# Revit family: IS_Cerasprint_B9576_BIM_FR
name_source: partatom
category: Plumbing Fixtures
revit_build: Autodesk Revit 2017 (Build: 20160225_1515(x64)
units: mm (PartAtom-declared; Revit-internal decimal feet)

## family parameters
Always vertical = No
Cut with Voids When Loaded = No
OmniClass Number = 23.45.55.17
OmniClass Title = Mixing Faucets
Part Type = Normal
Room Calculation Point = No
Round Connector Dimension = Use Diameter
Shared = No
Work Plane-Based = No

## types (1)
- B9576AA - CERASPRINT MIT EVIER BEC TUBE 230MM CHR
    Accessoires = www.idealspec.fr
    Auteur = Ideal Standard
    BIMobject category = Taps & Mixers
    BIMobject category code = kitchen-taps
    BIMobject main category = Kitchen
    BIMobject main category code = kitchen
    BOSUseNativeGeometries = 1
    Bim-NomDuProjet = ISI_IdealStandard_SinkWaterSupplyFittings_CERASPRINT_B9576AA
    Brand url = www.idealspec.fr
    Caractéristiques = CERASPRINT SNK MXR R-MTD TUB/SPT U230MM
    CodeBarre = 3800861026952
    Conformité = NF
    ConseilsDInstallation = 0
    Cost = 0 $
    Couleur = Chrome
    CoûtDeRemplacement = 0
    Date of publishing = 2018_07_24
    DateDeCréation = 2018_07_24
    Description = CERASPRINT Mitigeur évier monotrou
    Dimensions = 306 x 85 x 251mm
    EAN code = https://3800861026952
    Edition number = 1
    Espace = Interne
    Finition = Chrome
    Forme = Complexe
    Hauteur = 306 mm  [stored 1.00394 ft]
    IFC Classification = Sanitary Terminal
    IfcExportAs = FAUCETS
    IfcExportType = IfcValveType
    InformationsProduit = www.idealspec.fr
    Installation instructions = http://www.idealspec.fr
    Largeur = 85 mm
    Longueur = 251 mm
    Manufacturer name = Ideal Standard
    Marque = Ideal Standard
    Material main = Brass
    Matériel = Brass
    Model = B9576AA
    NBS Reference Code = 35-79-79
    NBS Reference Description = Sink Water Supply Fittings
    Nominal height = 306
    Nominal width = 84
    OmniClass Code = 23-31 11 00
    OmniClass Description = Faucets
    Product Guid = 93ca3ec0-5324-4a6a-9915-9a6a16119ddc
    Product SKU = B9576
    Product certification = http://www.idealspec.fr
    Product data url = https://bimobject.com
    Product family = CERASPRINT
    Product group = Kitchen Mixer
    Product name = CERASPRINT SNK MXR R-MTD TUB/SPT U230MM
    Product url = http://www.idealspec.fr
    Profondeur = 0 mm  [stored 0 ft]
    QR code = http://bimobject.com
    Raccordement = Plomberie
    Révision = 1
    Technical description = http://www.idealspec.fr
    TestDePression = 0
    TypeDeRobinetterie = Sink Mixer
    URL = www.idealspec.fr
    Uniclass 1.4 Code = L8212
    Uniclass 1.4 Description = Fittings
    Uniclass 2.0 Code = PR-35-79-79
    Uniclass 2.0 Description = Sink Water Supply Fittings
    Uniclass 2015 Code = Pr_40_20_87_82
    Uniclass 2015 Name = Sink manual water supply sets
    Uniclass2015Code = Pr_40_20_87_82
    Uniclass2015Title = Sink manual water supply sets
    Uniclass2015Version = Products v1.1
    UnitéDeMesure = Millimètres
    UnitéDeTemps = An
    UnitéMonétaire = €
    UrlDuFabricant = www.idealspec.fr
    Version = 1
    Weight Net (Kg) = 1.79
    Youtube clip = http://www.idealspec.fr

note: [stored X ft] marks values corroborated as IEEE doubles in the binary element streams (Revit-internal decimal feet)

## geometry (parser evidence)
native form markers: Sweep x2
no freeform markers — native parametric forms only
